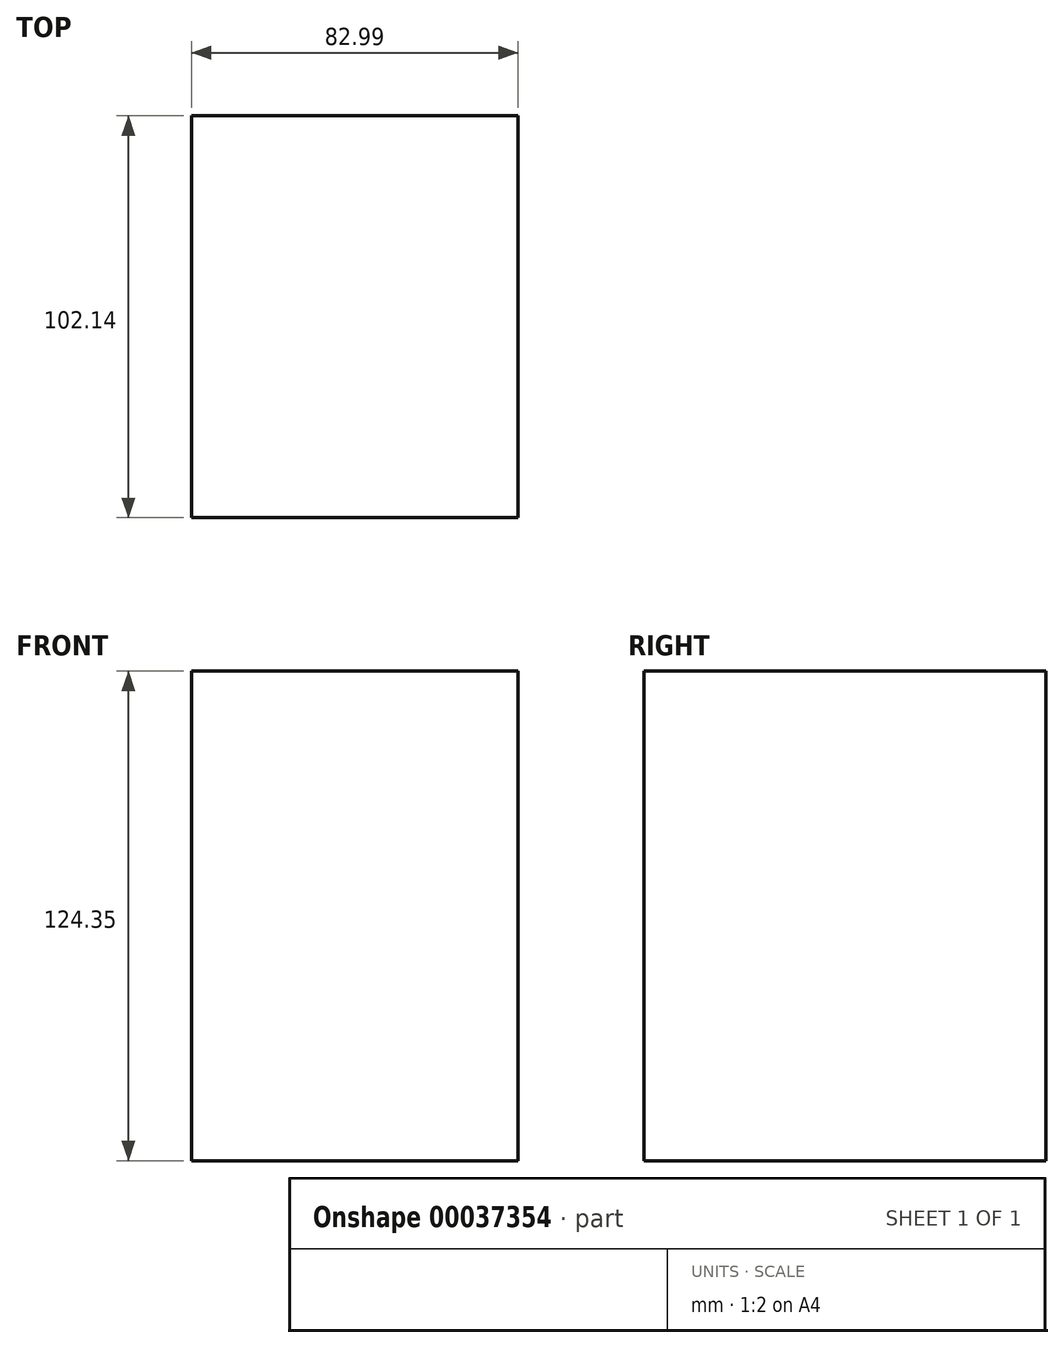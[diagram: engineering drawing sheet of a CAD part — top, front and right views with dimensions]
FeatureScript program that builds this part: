
annotation { "Feature Type Name" : "Feature", "Feature Type Description" : "" }
export const myFeature = defineFeature(function(context is Context, id is Id, definition is map)
    precondition{}
    {
        {
            var Q0;
            Q0=qCreatedBy(makeId("Top.planeOp"),FACE);
            var sketch = newSketch(context, id + "F0", { "sketchPlane" : qUnion([Q0])});
            skLineSegment(sketch, "E0", {"start": v(143.97, -45.33) * mm, "end": v(143.97, 56.8) * mm});
            skLineSegment(sketch, "E1", {"start": v(143.97, 56.8) * mm, "end": v(60.98, 56.8) * mm});
            skLineSegment(sketch, "E2", {"start": v(60.98, 56.8) * mm, "end": v(60.98, -45.33) * mm});
            skLineSegment(sketch, "E3", {"start": v(60.98, -45.33) * mm, "end": v(143.97, -45.33) * mm});
            skSolve(sketch);
        }
        {
            var Q0;
            Q0=makeQuery(id+"F0.imprint","IMPRINT",FACE,{"disambiguationData":[TD([[makeQuery(id+"F0.imprint","IMPRINT",EDGE,{"derivedFrom":sQuery(id+"F0.wireOp",EDGE,"E0")}),1.0]])]});
            extrude(context, id + "F1", {"entities" : qUnion([Q0]), "depth" : 98.95 * mm, "hasSecondDirection" : true, "secondDirectionOppositeDirection" : true, "secondDirectionDepth" : 25.4 * mm});
        }
    });
